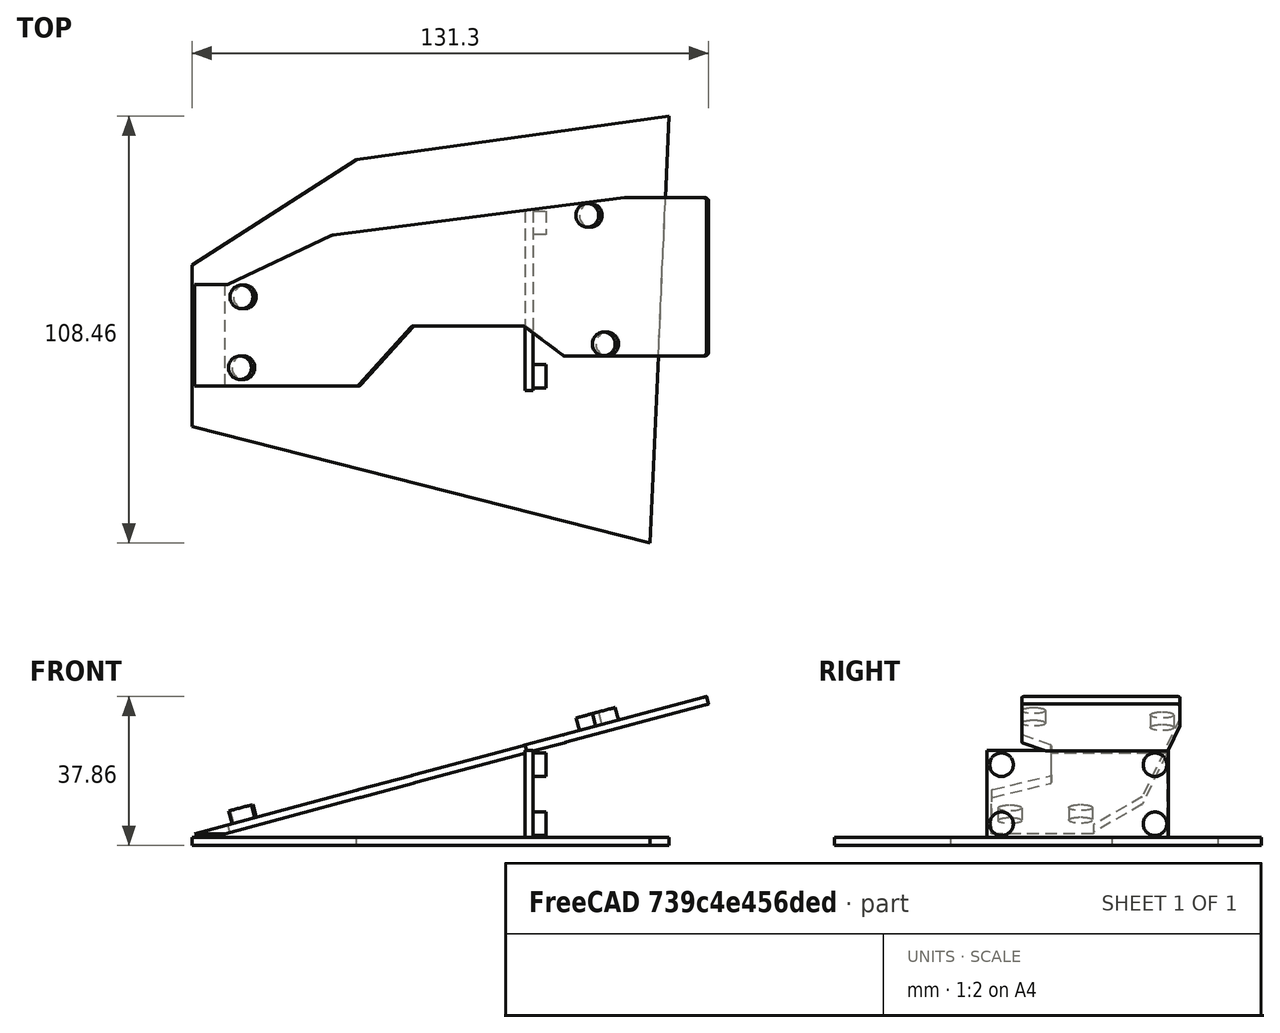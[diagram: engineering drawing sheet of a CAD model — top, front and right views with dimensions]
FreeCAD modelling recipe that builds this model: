
FCSTD DOCUMENT  (FreeCAD 1.0RUnknown)
Label: case-tent-nojoy
License: All rights reserved
LicenseURL: https://en.wikipedia.org/wiki/All_rights_reserved
objects: Sketcher::SketchObject×7, PartDesign::Pad×6, PartDesign::Plane×2, App::Link×2, App::FeaturePython×2, PartDesign::Body×1, App::Part×1, Assembly::JointGroup×1, Assembly::AssemblyObject×1
note: 35 computed .brp shape members not serialized (recipe doc carries the construction recipe); baked Part::Feature solids carry a one-line shape summary decoded from their .brp
EXTERNAL_REF file=left.FCStd obj=Board_f9e4

FEATURE [PartDesign::Plane] DatumPlane  label="tilt plane"
  AttachmentOffset = pos=(0,0,0) rot=(0,-1,0;0.261799rad)
  AttachmentSupport = -> [XY_Plane001]
  Length = 193.679
  MapMode = 5
  Placement = pos=(0,0,0) rot=(0,-1,0;0.261799rad)
  ResizeMode = 0
  Width = 135.367
FEATURE [Sketcher::SketchObject] PCB_Sketch_f9e006  label="left"
  ArcFitTolerance = 1e-06
  AttachmentOffset = pos=(0,3,4.4) rot=(0,0,1;0rad)
  AttachmentSupport = -> [DatumPlane]
  FullyConstrained = false
  MakeInternals = false
  MapMode = 5
  Placement = pos=(-1.1388,3,4.25007) rot=(0,-1,0;0.261799rad)
  sketch-geometry (22):
    g0: LineSegment StartX=48.9342 StartY=15.25 StartZ=0 EndX=77.5946 EndY=15.25 EndZ=0
    g1: LineSegment StartX=27.2503 StartY=38.2054 StartZ=0 EndX=0.008196 EndY=25.8215 EndZ=0
    g2: LineSegment StartX=126 StartY=8.65 StartZ=0 EndX=126 EndY=45.95 EndZ=0
    g3: LineSegment StartX=104.439 StartY=47.8424 StartZ=0 EndX=27.5489 EndY=38.289 EndZ=0
    g4: LineSegment StartX=34.5465 StartY=0.317255 StartZ=0 EndX=48.2035 EndY=14.9327 EndZ=0
    g5: LineSegment StartX=104.562 StartY=47.85 StartZ=0 EndX=125 EndY=47.85 EndZ=0
    g6: LineSegment StartX=125 StartY=7.65 StartZ=0 EndX=88.6266 EndY=7.65 EndZ=0
    g7: LineSegment StartX=0.008196 StartY=0 StartZ=0 EndX=33.8158 EndY=-1.6e-15 EndZ=0
    g8: LineSegment StartX=126 StartY=45.95 StartZ=0 EndX=126 EndY=46.85 EndZ=0
    g9: LineSegment StartX=78.291 StartY=14.9676 StartZ=0 EndX=88.0364 EndY=7.84274 EndZ=0
    g10: ArcOfCircle CenterX=27.666 CenterY=37.2959 CenterZ=0 NormalX=0 NormalY=0 NormalZ=-1 AngleXU=1.14211 Radius=1.00001 StartAngle=0 EndAngle=0.311303
    g11: ArcOfCircle CenterX=33.8158 CenterY=1.00002 CenterZ=0 NormalX=0 NormalY=0 NormalZ=-1 AngleXU=-2.39007 Radius=1.00002 StartAngle=0 EndAngle=0.81927
    g12: ArcOfCircle CenterX=48.9342 CenterY=14.25 CenterZ=0 NormalX=0 NormalY=0 NormalZ=-1 AngleXU=0.75152 Radius=1.00002 StartAngle=0 EndAngle=0.81927
    g13: ArcOfCircle CenterX=125 CenterY=46.85 CenterZ=0 NormalX=0 NormalY=0 NormalZ=-1 AngleXU=1.5708 Radius=0.999999 StartAngle=0 EndAngle=1.5708
    g14: ArcOfCircle CenterX=125 CenterY=8.65 CenterZ=0 NormalX=0 NormalY=0 NormalZ=-1 AngleXU=3.14159 Radius=0.999999 StartAngle=0 EndAngle=1.5708
    g15: ArcOfCircle CenterX=88.6266 CenterY=8.65 CenterZ=0 NormalX=0 NormalY=0 NormalZ=-1 AngleXU=-1.57079 Radius=1 StartAngle=0 EndAngle=0.631296
    g16: ArcOfCircle CenterX=104.562 CenterY=46.8498 CenterZ=0 NormalX=0 NormalY=0 NormalZ=-1 AngleXU=1.44719 Radius=1.00016 StartAngle=0 EndAngle=0.123594
    g17: ArcOfCircle CenterX=77.5946 CenterY=14.25 CenterZ=0 NormalX=0 NormalY=0 NormalZ=-1 AngleXU=1.57078 Radius=0.999961 StartAngle=0 EndAngle=0.770416
    g18: GeomPoint [constr] X=4.15 Y=4.65 Z=0
    g19: GeomPoint [constr] X=95.5 Y=43.35 Z=0
    g20: GeomPoint [constr] X=99.8333 Y=10.6833 Z=0
    g21: LineSegment StartX=0.008196 StartY=25.8215 StartZ=0 EndX=0.008196 EndY=0 EndZ=0
  constraints (20):
    c: Coincident(g1,g10)
    c: Coincident(g3,g10)
    c: Coincident(g7,g11)
    c: Coincident(g4,g11)
    c: Coincident(g4,g12)
    c: Coincident(g0,g12)
    c: Coincident(g0,g17)
    c: Coincident(g9,g17)
    c: Coincident(g9,g15)
    c: Coincident(g6,g15)
    c: Coincident(g3,g16)
    c: Coincident(g5,g16)
    c: Coincident(g6,g14)
    c: Coincident(g5,g13)
    c: Coincident(g2,g14)
    c: Coincident(g2,g8)
    c: Coincident(g8,g13)
    c: Coincident(g1,g21)
    c: Coincident(g21,g7)
    c: Vertical(g21)
FEATURE [PartDesign::Pad] Pad
  Direction = (-0.258819,0,0.965926)
  Length = 2
  Length2 = 10
  Placement = pos=(0,0,0) rot=(0,-1,0;0.261799rad)
  Profile = -> PCB_Sketch_f9e006
  ReferenceAxis = -> PCB_Sketch_f9e006 [N_Axis]
  Refine = true
  Reversed = true
  Suppressed = false
  Type = 0
FEATURE [PartDesign::Plane] DatumPlane001
  AttachmentOffset = pos=(0,0,2) rot=(0,0,1;0rad)
  AttachmentSupport = -> [XY_Plane001]
  Length = 180.277
  MapMode = 5
  Placement = pos=(0,0,2) rot=(0,0,1;0rad)
  ResizeMode = 0
  Width = 134.349
FEATURE [Sketcher::SketchObject] Sketch001
  ArcFitTolerance = 1e-06
  AttacherType = Attacher::AttachEngine3D
  AttachmentSupport = -> [Pad]
  FullyConstrained = false
  MakeInternals = false
  MapMode = 5
  Placement = pos=(0.00791673,0,0.00212128) rot=(0.621515,-0.621515,-0.476905;2.25159rad)
  sketch-geometry (4):
    g0: LineSegment StartX=-28.8215 StartY=4.4 StartZ=0 EndX=-28.8215 EndY=2.4 EndZ=0
    g1: LineSegment StartX=-28.8215 StartY=2.4 StartZ=0 EndX=-3 EndY=2.4 EndZ=0
    g2: LineSegment StartX=-3 StartY=2.4 StartZ=0 EndX=-3 EndY=4.4 EndZ=0
    g3: LineSegment StartX=-3 StartY=4.4 StartZ=0 EndX=-28.8215 EndY=4.4 EndZ=0
  constraints (8):
    c: Coincident(g0,g1)
    c: Coincident(g1,g2)
    c: Coincident(g2,g3)
    c: Coincident(g3,g0)
    c: Vertical(g0)
    c: Vertical(g2)
    c: Horizontal(g1)
    c: Horizontal(g3)
FEATURE [Sketcher::SketchObject] Sketch
  ArcFitTolerance = 1e-06
  AttachmentSupport = -> [XY_Plane001]
  FullyConstrained = false
  MakeInternals = false
  MapMode = 5
  sketch-geometry (5):
    g0: LineSegment StartX=-10.2101 StartY=33.6647 StartZ=0 EndX=-10.2101 EndY=-7.34119 EndZ=0
    g1: LineSegment StartX=-10.2101 StartY=-7.34119 StartZ=0 EndX=106.194 EndY=-36.883 EndZ=0
    g2: LineSegment StartX=106.194 StartY=-36.883 StartZ=0 EndX=111.044 EndY=71.5841 EndZ=0
    g3: LineSegment StartX=111.044 StartY=71.5841 StartZ=0 EndX=31.6776 EndY=60.561 EndZ=0
    g4: LineSegment StartX=31.6776 StartY=60.561 StartZ=0 EndX=-10.2101 EndY=33.6647 EndZ=0
  constraints (6):
    c: Vertical(g0)
    c: Coincident(g0,g1)
    c: Coincident(g1,g2)
    c: Coincident(g2,g3)
    c: Coincident(g3,g4)
    c: Coincident(g4,g0)
FEATURE [PartDesign::Pad] Pad003
  BaseFeature = -> Pad
  Direction = (0,0,1)
  Length = 2
  Length2 = 10
  Midplane = true
  Placement = pos=(0,0,0) rot=(0,-1,0;0.261799rad)
  Profile = -> Sketch
  ReferenceAxis = -> Sketch [N_Axis]
  Refine = true
  Suppressed = false
  Type = 0
FEATURE [Sketcher::SketchObject] Sketch002
  ArcFitTolerance = 1e-06
  AttachmentSupport = -> [XY_Plane001]
  ExternalGeometry = -> [PCB_Sketch_f9e006]
  FullyConstrained = false
  MakeInternals = false
  MapMode = 5
  sketch-geometry (5):
    g0: LineSegment StartX=74.4845 StartY=17.9676 StartZ=0 EndX=74.4845 EndY=1.83853 EndZ=0
    g1: LineSegment StartX=74.4845 StartY=1.83853 StartZ=0 EndX=76.4845 EndY=1.83853 EndZ=0
    g2: LineSegment StartX=76.4845 StartY=1.83853 StartZ=0 EndX=76.4845 EndY=47.8508 EndZ=0
    g3: LineSegment StartX=76.4845 StartY=47.8508 StartZ=0 EndX=74.4845 EndY=47.5936 EndZ=0
    g4: LineSegment StartX=74.4845 StartY=47.5936 StartZ=0 EndX=74.4845 EndY=17.9676 EndZ=0
  constraints (13):
    c: Coincident(g-3,g0)
    c: Vertical(g0)
    c: Coincident(g0,g1)
    c: Horizontal(g1)
    c: Coincident(g1,g2)
    c: PointOnObject(g2,g-4)
    c: Vertical(g2)
    c: Coincident(g2,g3)
    c: PointOnObject(g3,g-4)
    c: Coincident(g3,g4)
    c: Coincident(g4,g0)
    c: Vertical(g4)
    c: DistanceX(g1,g1) = 2
FEATURE [PartDesign::Pad] Pad004
  BaseFeature = -> Pad003
  Direction = (0,0,1)
  Length = 23.1
  Length2 = 10
  Placement = pos=(0,0,0) rot=(0,-1,0;0.261799rad)
  Profile = -> Sketch002
  ReferenceAxis = -> Sketch002 [N_Axis]
  Refine = true
  Suppressed = false
  Type = 0
FEATURE [Sketcher::SketchObject] PCB_Sketch_58ce  label="thumb cluster"
  ArcFitTolerance = 1e-06
  AttachmentOffset = pos=(2.5,22.5,0) rot=(0,0,1;-1.5708rad)
  AttachmentSupport = -> [Pad004]
  FullyConstrained = false
  MakeInternals = false
  MapMode = 5
  Placement = pos=(76.4845,2.5,22.5) rot=(0,-1,0;4.71239rad)
  sketch-geometry (16):
    g0: LineSegment StartX=21 StartY=44 StartZ=0 EndX=21 EndY=1 EndZ=0
    g1: LineSegment StartX=20 StartY=1e-16 StartZ=0 EndX=1 EndY=0 EndZ=0
    g2: LineSegment StartX=1 StartY=45 StartZ=0 EndX=20 EndY=45 EndZ=0
    g3: LineSegment StartX=1e-16 StartY=1 StartZ=0 EndX=3.3e-15 EndY=44 EndZ=0
    g4: ArcOfCircle CenterX=20 CenterY=44 CenterZ=0 NormalX=0 NormalY=0 NormalZ=-1 AngleXU=1.5708 Radius=0.999999 StartAngle=0 EndAngle=1.5708
    g5: ArcOfCircle CenterX=0.999999 CenterY=0.999999 CenterZ=0 NormalX=0 NormalY=0 NormalZ=-1 AngleXU=-1.5708 Radius=0.999999 StartAngle=0 EndAngle=1.5708
    g6: ArcOfCircle CenterX=20 CenterY=0.999999 CenterZ=0 NormalX=0 NormalY=0 NormalZ=-1 AngleXU=3.14159 Radius=0.999999 StartAngle=0 EndAngle=1.5708
    g7: ArcOfCircle CenterX=0.999999 CenterY=44 CenterZ=0 NormalX=0 NormalY=0 NormalZ=-1 AngleXU=-7.47076e-07 Radius=0.999999 StartAngle=0 EndAngle=1.5708
    g8: GeomPoint [constr] X=3 Y=42 Z=0
    g9: GeomPoint [constr] X=18 Y=42 Z=0
    g10: GeomPoint [constr] X=18 Y=3 Z=0
    g11: GeomPoint [constr] X=3 Y=3 Z=0
    g12: Circle CenterX=3 CenterY=42 CenterZ=0 NormalX=0 NormalY=0 NormalZ=1 AngleXU=0 Radius=3
    g13: Circle CenterX=18 CenterY=42 CenterZ=0 NormalX=0 NormalY=0 NormalZ=1 AngleXU=0 Radius=3
    g14: Circle CenterX=18 CenterY=3 CenterZ=0 NormalX=0 NormalY=0 NormalZ=1 AngleXU=0 Radius=3
    g15: Circle CenterX=3 CenterY=3 CenterZ=0 NormalX=0 NormalY=0 NormalZ=1 AngleXU=0 Radius=3
  constraints (18):
    c: Coincident(g3,g5)
    c: Coincident(g3,g7)
    c: Coincident(g1,g5)
    c: Coincident(g2,g7)
    c: Coincident(g1,g6)
    c: Coincident(g2,g4)
    c: Coincident(g0,g6)
    c: Coincident(g0,g4)
    c: Diameter(g12) = 6
    c: Coincident(g12,g8)
    c: Diameter(g13) = 6
    c: Coincident(g13,g9)
    c: Tangent(g13,g0)
    c: Diameter(g14) = 6
    c: Coincident(g14,g10)
    c: Tangent(g14,g0)
    c: Diameter(g15) = 6
    c: Coincident(g15,g11)
FEATURE [Sketcher::SketchObject] Sketch004
  ArcFitTolerance = 1e-06
  AttacherType = Attacher::AttachEngine3D
  AttachmentSupport = -> [Pad004]
  ExternalGeometry = -> [PCB_Sketch_58ce]
  FullyConstrained = true
  MakeInternals = false
  MapMode = 5
  Placement = pos=(76.4845,0,-4.2e-15) rot=(0.57735,0.57735,0.57735;2.0944rad)
  sketch-geometry (4):
    g0: Circle CenterX=5.5 CenterY=19.5 CenterZ=0 NormalX=0 NormalY=0 NormalZ=1 AngleXU=0 Radius=3
    g1: Circle CenterX=44.5 CenterY=19.5 CenterZ=0 NormalX=0 NormalY=0 NormalZ=1 AngleXU=0 Radius=3
    g2: Circle CenterX=44.5 CenterY=4.5 CenterZ=0 NormalX=0 NormalY=0 NormalZ=1 AngleXU=0 Radius=3
    g3: Circle CenterX=5.5 CenterY=4.5 CenterZ=0 NormalX=0 NormalY=0 NormalZ=1 AngleXU=0 Radius=3
  constraints (8):
    c: Coincident(g0,g-3)
    c: Equal(g0,g-3)
    c: Coincident(g1,g-4)
    c: Equal(g1,g-4)
    c: Coincident(g2,g-5)
    c: Equal(g2,g-5)
    c: Coincident(g3,g-6)
    c: Equal(g3,g-6)
FEATURE [PartDesign::Pad] Pad006
  BaseFeature = -> Pad004
  Direction = (1,0,0)
  Length = 3.3
  Length2 = 10
  Placement = pos=(0,0,0) rot=(0,-1,0;0.261799rad)
  Profile = -> Sketch004
  ReferenceAxis = -> Sketch004 [N_Axis]
  Refine = true
  Suppressed = false
  Type = 0
FEATURE [PartDesign::Pad] Pad007
  BaseFeature = -> Pad006
  Direction = (-0.965926,-1e-16,-0.258819)
  Length = 10
  Length2 = 10
  Placement = pos=(0,0,0) rot=(0,-1,0;0.261799rad)
  Profile = -> Sketch001
  ReferenceAxis = -> Sketch001 [N_Axis]
  Refine = true
  Suppressed = false
  Type = 3
  UpToFace = -> DatumPlane001
FEATURE [Sketcher::SketchObject] Sketch005
  ArcFitTolerance = 1e-06
  AttachmentSupport = -> [Pad007]
  FullyConstrained = false
  MakeInternals = false
  MapMode = 5
  Placement = pos=(-1.1388,-1e-16,4.25007) rot=(0,-1,0;0.261799rad)
  sketch-geometry (4):
    g0: Circle CenterX=95.5 CenterY=46.35 CenterZ=0 NormalX=0 NormalY=0 NormalZ=1 AngleXU=0 Radius=3
    g1: Circle CenterX=99.8333 CenterY=13.6833 CenterZ=0 NormalX=0 NormalY=0 NormalZ=1 AngleXU=0 Radius=3
    g2: Circle CenterX=4.5434 CenterY=25.6249 CenterZ=0 NormalX=0 NormalY=0 NormalZ=1 AngleXU=0 Radius=3
    g3: Circle CenterX=4.15 CenterY=7.65 CenterZ=0 NormalX=0 NormalY=0 NormalZ=1 AngleXU=0 Radius=3
  constraints (4):
    c: Diameter(g0) = 6
    c: Diameter(g1) = 6
    c: Diameter(g2) = 6
    c: Diameter(g3) = 6
FEATURE [PartDesign::Pad] Pad008
  BaseFeature = -> Pad007
  Direction = (-0.258819,0,0.965926)
  Length = 3.3
  Length2 = 10
  Placement = pos=(0,0,0) rot=(0,-1,0;0.261799rad)
  Profile = -> Sketch005
  ReferenceAxis = -> Sketch005 [N_Axis]
  Refine = true
  Suppressed = false
  Type = 0
FEATURE [PartDesign::Body] Body
  AllowCompound = true
  Group = -> [DatumPlane,PCB_Sketch_f9e006,Pad,PCB_Sketch_58ce,DatumPlane001,Sketch001,Sketch,Pad003,Sketch002,Pad004,Sketch004,Pad006,Pad007,Sketch005,Pad008]
  Origin = -> Origin001
  Tip = -> Pad008
FEATURE [App::Part] Part
  Group = -> [Body]
  Origin = -> Origin
FEATURE [App::Link] Part001
  LinkPlacement = pos=(25.9529,-535.714,222.029) rot=(0,0,1;0rad)
  LinkedObject = -> Part
  Placement = pos=(25.9529,-535.714,222.029) rot=(0,0,1;0rad)
FEATURE [App::FeaturePython] GroundedJoint  # Assembly grounded joint (typed FeaturePython)
  ObjectToGround = -> Part001
  Placement = pos=(25.9529,-535.714,222.029) rot=(0,0,1;0rad)
FEATURE [App::Link] left  label="left001"
  LinkPlacement = pos=(23.5459,-532.714,231.012) rot=(0,-1,0;0.261799rad)
  LinkedObject = -> <external left.FCStd>#Board_f9e4
  Placement = pos=(23.5459,-532.714,231.012) rot=(0,-1,0;0.261799rad)
FEATURE [App::FeaturePython] Joint  label="Fixed"  # Assembly joint (typed FeaturePython)
  Activated = true
  AngleMax = 0
  AngleMin = 0
  Detach1 = false
  Detach2 = false
  Distance = 0
  Distance2 = 0
  EnableAngleMax = false
  EnableAngleMin = false
  EnableLengthMax = false
  EnableLengthMin = false
  JointType = 0 (Fixed)
  LengthMax = 0
  LengthMin = 0
  Placement1 = pos=(119.333,-97.1667,-1.6) rot=(0,0,1;0rad)
  Placement2 = pos=(94.4386,13.6833,33.2764) rot=(0,-1,0;0.261799rad)
  Reference1 = -> Assembly [left.Board_Geoms_f9e4.Pcb_f9e4.Edge129,left.Board_Geoms_f9e4.Pcb_f9e4.Edge129]
  Reference2 = -> Assembly [Part001.Body.Edge76,Part001.Body.Edge76]
FEATURE [Assembly::JointGroup] Joints
  Group = -> [GroundedJoint,Joint]
FEATURE [Assembly::AssemblyObject] Assembly
  Group = -> [Joints,Part001,GroundedJoint,left,Joint]
  Origin = -> Origin002
  Type = Assembly

RESOLVED EXTERNAL PARTS (link-assembly join: the EXTERNAL_REF files above that resolve inside this repo's crawl, each included once):
---- part left.FCStd = doc fcstd_3019e020500d (78541 chars; too large to inline — full recipe in that document) ----
